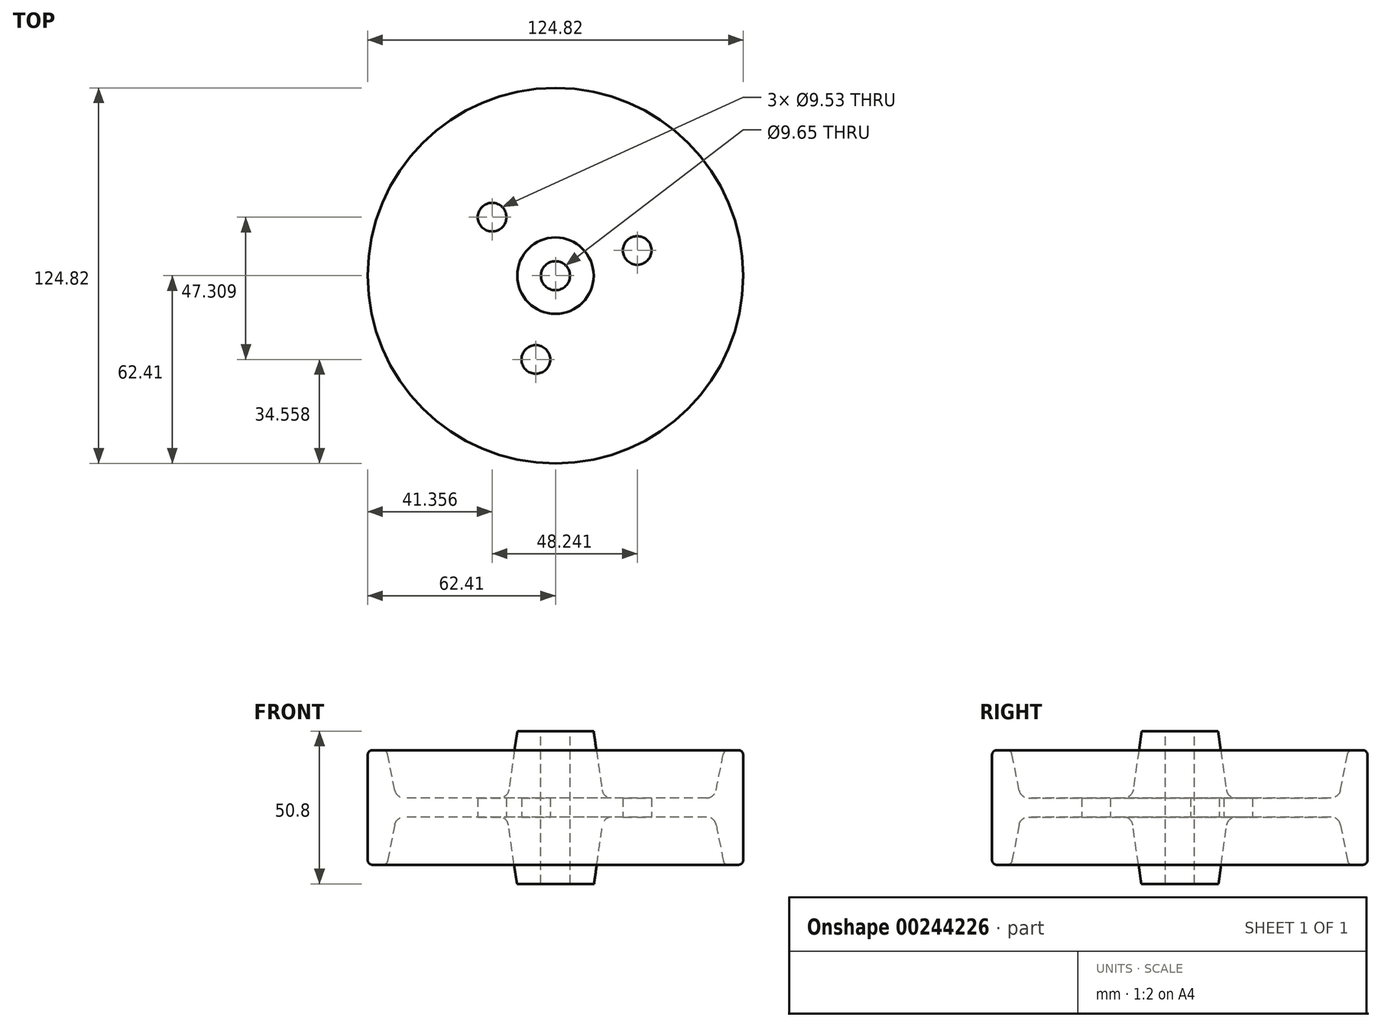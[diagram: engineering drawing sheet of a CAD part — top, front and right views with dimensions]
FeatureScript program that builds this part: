
annotation { "Feature Type Name" : "Feature", "Feature Type Description" : "" }
export const myFeature = defineFeature(function(context is Context, id is Id, definition is map)
    precondition{}
    {
        {
            var Q0;
            Q0=qCreatedBy(makeId("Front.planeOp"),FACE);
            var sketch = newSketch(context, id + "F0", { "sketchPlane" : qUnion([Q0])});
            skLineSegment(sketch, "E0", {"start": v(-119.75, 31.4) * mm, "end": v(-119.75, 13.95) * mm});
            skLineSegment(sketch, "E1", {"start": v(-118.16, 33) * mm, "end": v(-114.7, 33) * mm});
            skLineSegment(sketch, "E2", {"start": v(-113.15, 31.72) * mm, "end": v(-110.74, 19.67) * mm});
            skLineSegment(sketch, "E3", {"start": v(-107.62, 17.12) * mm, "end": v(-75.97, 17.12) * mm});
            skLineSegment(sketch, "E4", {"start": v(-57.34, 33.85) * mm, "end": v(-57.34, 19.47) * mm});
            skLineSegment(sketch, "E5", {"start": v(-72.83, 19.85) * mm, "end": v(-70.04, 39.35) * mm});
            skLineSegment(sketch, "E6", {"start": v(-70.04, 39.35) * mm, "end": v(-62.17, 39.35) * mm});
            skLineSegment(sketch, "E7", {"start": v(-62.17, 39.35) * mm, "end": v(-62.17, 13.95) * mm});
            skPoint(sketch, "E8.visualSharp", {"position": v(-110.23, 17.12) * mm});
            skArc(sketch, "E8.filletArc", {"start": v(-110.74, 19.67) * mm, "mid": v(-109.64, 17.84) * mm, "end": v(-107.62, 17.12) * mm});
            skPoint(sketch, "E9.visualSharp", {"position": v(-73.21, 17.12) * mm});
            skArc(sketch, "E9.filletArc", {"start": v(-75.97, 17.12) * mm, "mid": v(-73.89, 17.9) * mm, "end": v(-72.83, 19.85) * mm});
            skPoint(sketch, "E10.visualSharp", {"position": v(-119.75, 33) * mm});
            skArc(sketch, "E10.filletArc", {"start": v(-118.16, 33) * mm, "mid": v(-119.29, 32.53) * mm, "end": v(-119.75, 31.4) * mm});
            skPoint(sketch, "E11.visualSharp", {"position": v(-113.4, 33) * mm});
            skArc(sketch, "E11.filletArc", {"start": v(-113.15, 31.72) * mm, "mid": v(-113.7, 32.64) * mm, "end": v(-114.7, 33) * mm});
            skArc(sketch, "E12.MirrorCS", {"start": v(-118.16, -5.1) * mm, "mid": v(-119.29, -4.64) * mm, "end": v(-119.75, -3.52) * mm});
            skArc(sketch, "E13.MirrorCS", {"start": v(-113.15, -3.83) * mm, "mid": v(-113.7, -4.74) * mm, "end": v(-114.7, -5.1) * mm});
            skLineSegment(sketch, "E14.MirrorCS", {"start": v(-70.17, -11.45) * mm, "end": v(-62.17, -11.45) * mm});
            skArc(sketch, "E15.MirrorCS", {"start": v(-110.74, 8.22) * mm, "mid": v(-109.64, 10.05) * mm, "end": v(-107.62, 10.77) * mm});
            skArc(sketch, "E16.MirrorCS", {"start": v(-76.1, 10.77) * mm, "mid": v(-74.01, 10) * mm, "end": v(-72.95, 8.05) * mm});
            skPoint(sketch, "E17.MirrorP", {"position": v(-113.4, -5.1) * mm});
            skLineSegment(sketch, "E18.MirrorCS", {"start": v(-62.17, -11.45) * mm, "end": v(-62.17, 13.95) * mm});
            skLineSegment(sketch, "E19.MirrorCS", {"start": v(-113.15, -3.83) * mm, "end": v(-110.74, 8.22) * mm});
            skPoint(sketch, "E20.MirrorP", {"position": v(-73.34, 10.77) * mm});
            skPoint(sketch, "E21.MirrorP", {"position": v(-110.23, 10.77) * mm});
            skPoint(sketch, "E22.MirrorP", {"position": v(-119.75, -5.1) * mm});
            skLineSegment(sketch, "E23.MirrorCS", {"start": v(-72.95, 8.05) * mm, "end": v(-70.17, -11.45) * mm});
            skLineSegment(sketch, "E24.MirrorCS", {"start": v(-119.75, -3.52) * mm, "end": v(-119.75, 13.95) * mm});
            skLineSegment(sketch, "E25.MirrorCS", {"start": v(-107.62, 10.77) * mm, "end": v(-76.1, 10.77) * mm});
            skLineSegment(sketch, "E26.MirrorCS", {"start": v(-118.16, -5.1) * mm, "end": v(-114.7, -5.1) * mm});
            skSolve(sketch);
        }
        {
            var Q0;
            Q0=makeQuery(id+"F0.imprint","IMPRINT",FACE,{"disambiguationData":[TD([[makeQuery(id+"F0.imprint","IMPRINT",EDGE,{"derivedFrom":sQuery(id+"F0.wireOp",EDGE,"E0")}),1.0]])]});
            var Q1;
            Q1=sQuery(id+"F0.wireOp",EDGE,"E4");
            revolve(context, id + "F1", {"entities" : qUnion([Q0]), "axis" : qUnion([Q1]), "revolveType" : RevolveType.FULL});
        }
        {
            var Q0;
            Q0=makeQuery(id+"F1.opRevolve","SWEPT_FACE",FACE,{"disambiguationData":[OSD([sQuery(id+"F0.wireOp",EDGE,"E25.MirrorCS")])]});
            var sketch = newSketch(context, id + "F2", { "sketchPlane" : qUnion([Q0])});
            skPoint(sketch, "E27", {"position": v(-78.4, -19.46) * mm});
            skPoint(sketch, "E28", {"position": v(-63.85, 27.85) * mm});
            skPoint(sketch, "E29", {"position": v(-30.15, -8.4) * mm});
            skCircle(sketch, "E30", {"center": v(-78.4, -19.46) * mm, "radius": 4.76 * mm});
            skCircle(sketch, "E31", {"center": v(-63.85, 27.85) * mm, "radius": 4.76 * mm});
            skCircle(sketch, "E32", {"center": v(-30.15, -8.4) * mm, "radius": 4.76 * mm});
            skPoint(sketch, "E33.center.orphan", {"position": v(-57.34, 0) * mm});
            skSolve(sketch);
        }
        {
            var Q0;
            Q0=sQuery(id+"F2.wireOp",VERTEX,"E27");
            var Q1;
            Q1=makeQuery(id+"F1.opRevolve","SWEPT_BODY",BODY,{"disambiguationData":[OSD([sQuery(id+"F0.wireOp",EDGE,"E0"),sQuery(id+"F0.wireOp",EDGE,"E1"),sQuery(id+"F0.wireOp",EDGE,"E2"),sQuery(id+"F0.wireOp",EDGE,"E3"),sQuery(id+"F0.wireOp",EDGE,"E5"),sQuery(id+"F0.wireOp",EDGE,"E6"),sQuery(id+"F0.wireOp",EDGE,"E7"),sQuery(id+"F0.wireOp",EDGE,"E8.filletArc"),sQuery(id+"F0.wireOp",EDGE,"E9.filletArc"),sQuery(id+"F0.wireOp",EDGE,"E10.filletArc"),sQuery(id+"F0.wireOp",EDGE,"E11.filletArc"),sQuery(id+"F0.wireOp",EDGE,"E12.MirrorCS"),sQuery(id+"F0.wireOp",EDGE,"E13.MirrorCS"),sQuery(id+"F0.wireOp",EDGE,"E14.MirrorCS"),sQuery(id+"F0.wireOp",EDGE,"E15.MirrorCS"),sQuery(id+"F0.wireOp",EDGE,"E16.MirrorCS"),sQuery(id+"F0.wireOp",EDGE,"E18.MirrorCS"),sQuery(id+"F0.wireOp",EDGE,"E19.MirrorCS"),sQuery(id+"F0.wireOp",EDGE,"E23.MirrorCS"),sQuery(id+"F0.wireOp",EDGE,"E24.MirrorCS"),sQuery(id+"F0.wireOp",EDGE,"E25.MirrorCS"),sQuery(id+"F0.wireOp",EDGE,"E26.MirrorCS")])]});
            hole(context, id + "F3", {"style" : HoleStyle.SIMPLE, "endStyle" : HoleEndStyle.THROUGH, "holeDiameter" : 9.52 * mm, "locations" : qUnion([Q0]), "scope" : qUnion([Q1]), "isTappedThrough" : true});
        }
        {
            var Q0;
            Q0=sQuery(id+"F2.wireOp",VERTEX,"E29");
            var Q1;
            Q1=makeQuery(id+"F1.opRevolve","SWEPT_BODY",BODY,{"disambiguationData":[OSD([sQuery(id+"F0.wireOp",EDGE,"E0"),sQuery(id+"F0.wireOp",EDGE,"E1"),sQuery(id+"F0.wireOp",EDGE,"E2"),sQuery(id+"F0.wireOp",EDGE,"E3"),sQuery(id+"F0.wireOp",EDGE,"E5"),sQuery(id+"F0.wireOp",EDGE,"E6"),sQuery(id+"F0.wireOp",EDGE,"E7"),sQuery(id+"F0.wireOp",EDGE,"E8.filletArc"),sQuery(id+"F0.wireOp",EDGE,"E9.filletArc"),sQuery(id+"F0.wireOp",EDGE,"E10.filletArc"),sQuery(id+"F0.wireOp",EDGE,"E11.filletArc"),sQuery(id+"F0.wireOp",EDGE,"E12.MirrorCS"),sQuery(id+"F0.wireOp",EDGE,"E13.MirrorCS"),sQuery(id+"F0.wireOp",EDGE,"E14.MirrorCS"),sQuery(id+"F0.wireOp",EDGE,"E15.MirrorCS"),sQuery(id+"F0.wireOp",EDGE,"E16.MirrorCS"),sQuery(id+"F0.wireOp",EDGE,"E18.MirrorCS"),sQuery(id+"F0.wireOp",EDGE,"E19.MirrorCS"),sQuery(id+"F0.wireOp",EDGE,"E23.MirrorCS"),sQuery(id+"F0.wireOp",EDGE,"E24.MirrorCS"),sQuery(id+"F0.wireOp",EDGE,"E25.MirrorCS"),sQuery(id+"F0.wireOp",EDGE,"E26.MirrorCS")])]});
            hole(context, id + "F4", {"style" : HoleStyle.SIMPLE, "endStyle" : HoleEndStyle.THROUGH, "holeDiameter" : 9.52 * mm, "locations" : qUnion([Q0]), "scope" : qUnion([Q1]), "isTappedThrough" : true});
        }
        {
            var Q0;
            Q0=sQuery(id+"F2.wireOp",VERTEX,"E28");
            var Q1;
            Q1=makeQuery(id+"F1.opRevolve","SWEPT_BODY",BODY,{"disambiguationData":[OSD([sQuery(id+"F0.wireOp",EDGE,"E0"),sQuery(id+"F0.wireOp",EDGE,"E1"),sQuery(id+"F0.wireOp",EDGE,"E2"),sQuery(id+"F0.wireOp",EDGE,"E3"),sQuery(id+"F0.wireOp",EDGE,"E5"),sQuery(id+"F0.wireOp",EDGE,"E6"),sQuery(id+"F0.wireOp",EDGE,"E7"),sQuery(id+"F0.wireOp",EDGE,"E8.filletArc"),sQuery(id+"F0.wireOp",EDGE,"E9.filletArc"),sQuery(id+"F0.wireOp",EDGE,"E10.filletArc"),sQuery(id+"F0.wireOp",EDGE,"E11.filletArc"),sQuery(id+"F0.wireOp",EDGE,"E12.MirrorCS"),sQuery(id+"F0.wireOp",EDGE,"E13.MirrorCS"),sQuery(id+"F0.wireOp",EDGE,"E14.MirrorCS"),sQuery(id+"F0.wireOp",EDGE,"E15.MirrorCS"),sQuery(id+"F0.wireOp",EDGE,"E16.MirrorCS"),sQuery(id+"F0.wireOp",EDGE,"E18.MirrorCS"),sQuery(id+"F0.wireOp",EDGE,"E19.MirrorCS"),sQuery(id+"F0.wireOp",EDGE,"E23.MirrorCS"),sQuery(id+"F0.wireOp",EDGE,"E24.MirrorCS"),sQuery(id+"F0.wireOp",EDGE,"E25.MirrorCS"),sQuery(id+"F0.wireOp",EDGE,"E26.MirrorCS")])]});
            hole(context, id + "F5", {"style" : HoleStyle.SIMPLE, "endStyle" : HoleEndStyle.THROUGH, "holeDiameter" : 9.52 * mm, "locations" : qUnion([Q0]), "scope" : qUnion([Q1]), "isTappedThrough" : true});
        }
    });
